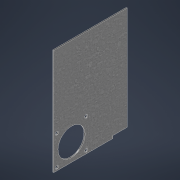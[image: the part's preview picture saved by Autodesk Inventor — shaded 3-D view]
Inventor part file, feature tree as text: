
AUTODESK INVENTOR PART (.ipt)
format: ipt  version: 2022 (Build 260153000, 153)  size: 132,608 bytes
history: native  units: mm (DEFAULTED — no unit token found)
features: other x10, extrude x2, sketch x2, reference x1
bodies: Body1 (feature_tree)
feature tree (15):
  other  "Sólido1"
  other  "Origen"
  extrude  "Extrusión1"  Depth=115.0mm
  extrude  "Extrusion2"  Depth=40.0mm
  other  "Plano YZ"
  other  "Plano XZ"
  other  "Plano XY"
  other  "Eje X"
  other  "Eje Y"
  other  "Eje Z"
  sketch  "Boceto1"  dims[d0=75.0mm d1=115.0mm]
  sketch  "Sketch2"  dims[d11=9.0mm d12=9.0mm d13=9.0mm d14=9.0mm d15=90.0deg d16=90.0deg d17=90.0deg d25=2.0mm d26=0.0mm d27=82.0mm d28=243.0mm d29=203.0mm d30=49.0mm d31=8.0mm d32=8.0mm d33=12.5mm d34=12.5mm d35=20.0mm d36=58.0mm d37=45.0deg d38=8.0mm d39=8.0mm d41=58.0mm d42=12.5mm d43=12.5mm d44=20.0mm d45=40.0mm d46=40.0mm d47=0.0mm d48=0.0mm]
  reference  "Reference1"
  other  "RobotPallet.iam"
  other  "PlanchaBaseInferior:1"
